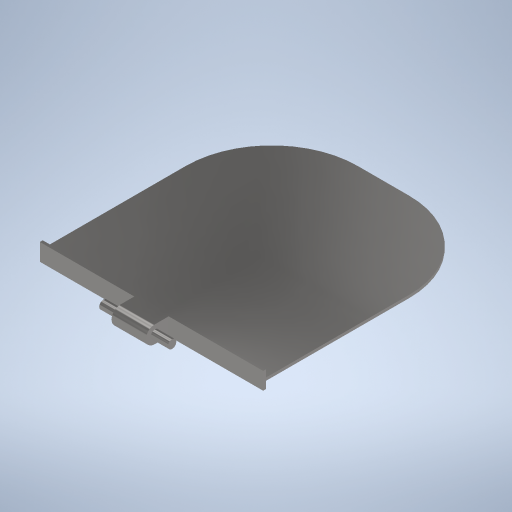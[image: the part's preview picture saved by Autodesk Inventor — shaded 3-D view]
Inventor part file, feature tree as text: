
AUTODESK INVENTOR PART (.ipt)
format: ipt  version: 2024 (Build 280153000, 153)  size: 287,744 bytes
history: native  units: mm
features: other x3, extrude x3, fillet x1, mirror x1
ambient origin geometry x8: Origin, YZ Plane, XZ Plane, XY Plane, X Axis, Y Axis, Z Axis, Center Point
bodies: Solid1 (feature_tree)
feature tree (8):
  other  "panel_sketch"
  extrude  "panel_extrude"  Depth=400.0mm
  other  "hinge_sketch"
  extrude  "hinge_extrude"  Depth=390.0mm
  fillet  "hinge_bottom_fillet"  Radius=250.0mm
  other  "hinge_link_sketch"
  extrude  "hinge_link_extrude"  Depth=45.0mm
  mirror  "hinge_link_extrude_mirror"
